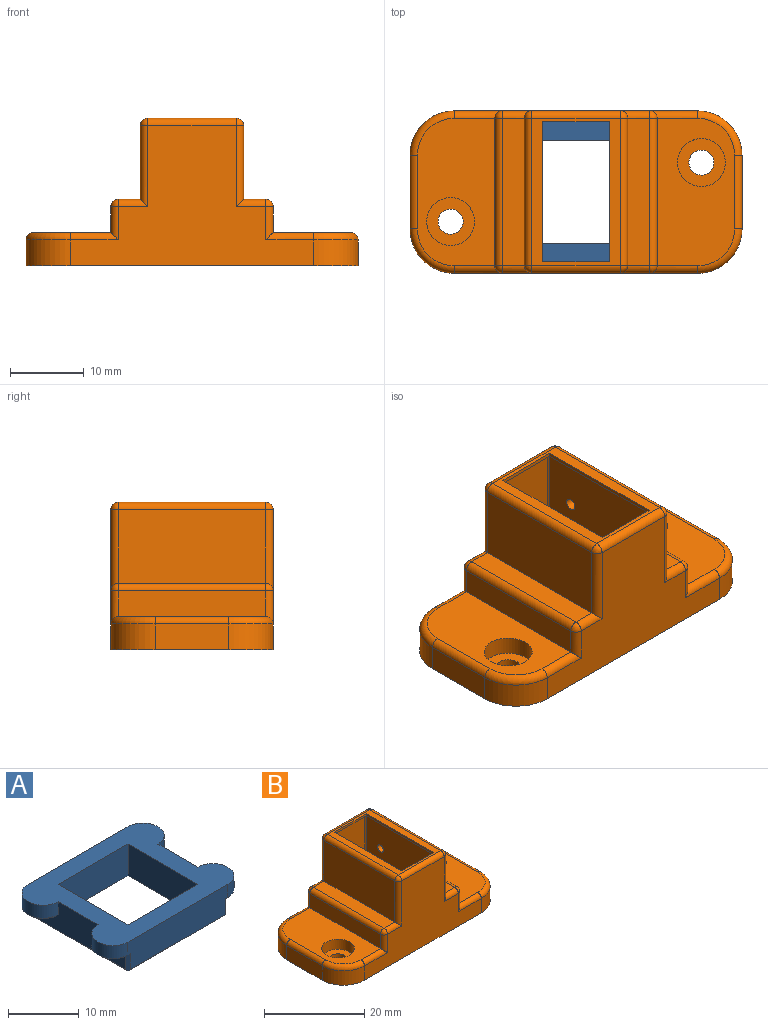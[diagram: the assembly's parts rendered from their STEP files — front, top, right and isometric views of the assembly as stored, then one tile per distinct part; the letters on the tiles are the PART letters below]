
ASSEMBLY  parts=2 mates=1
PART A: 42 faces, bbox 26x20x5.5 mm
  f0: plane 26x20mm, normal (0,0,1), area 260.5mm2, adj f5,f6,f7,f8,f9,f10,f11,f12
  f1: plane 19x19mm, normal (0,0,-1), area 165mm2, adj f22,f23,f24,f25,f26,f27,f28,f29
  f2: plane 5.5x3mm, normal (0,0,-1), area 8.1mm2, adj f12,f17,f31,f34,f35
  f3: plane 5.5x3mm, normal (0,0,-1), area 8.1mm2, adj f8,f15,f30,f38,f39
  f4: plane 5.5x3mm, normal (0,0,-1), area 8.1mm2, adj f8,f21,f32,f40,f41
  f5: cylinder r=3mm len=6mm, axis (0,0,-1), area 21.2mm2, adj f0,f6,f12,f36
  f6: plane 20x5mm, normal (0,1,0), area 97.2mm2, adj f0,f5,f7,f28,f32,f33,f37,f41
  f7: cylinder r=3mm len=6mm, axis (0,0,-1), area 21.2mm2, adj f0,f6,f8,f40
  f8: plane 19x5mm, normal (-1,0,0), area 67.6mm2, adj f0,f3,f4,f7,f9,f29,f30,f32
  f9: cylinder r=3mm len=6mm, axis (0,0,-1), area 21.2mm2, adj f0,f8,f10,f38
  f10: plane 20x5mm, normal (0,-1,0), area 97.2mm2, adj f0,f9,f11,f27,f30,f31,f35,f39
  f11: cylinder r=3mm len=6mm, axis (0,0,-1), area 21.2mm2, adj f0,f10,f12,f34
  f12: plane 19x5mm, normal (1,0,0), area 67.6mm2, adj f0,f2,f5,f11,f13,f26,f31,f33
  f13: plane 5.5x3mm, normal (0,0,-1), area 8.1mm2, adj f12,f19,f33,f36,f37
  f14: cone r=0mm half-angle=59deg, axis (0,0,-1), area 4.4mm2, adj f15
  f15: cylinder r=1.1mm len=2.2mm, axis (0,0,-1), area 3.5mm2, adj f3,f14
  f16: cone r=0mm half-angle=59deg, axis (0,0,-1), area 4.4mm2, adj f17
  f17: cylinder r=1.1mm len=2.2mm, axis (0,0,-1), area 3.5mm2, adj f2,f16
  f18: cone r=0mm half-angle=59deg, axis (0,0,-1), area 4.4mm2, adj f19
  f19: cylinder r=1.1mm len=2.2mm, axis (0,0,-1), area 3.5mm2, adj f13,f18
  f20: cone r=0mm half-angle=59deg, axis (0,0,-1), area 4.4mm2, adj f21
  f21: cylinder r=1.1mm len=2.2mm, axis (0,0,-1), area 3.5mm2, adj f4,f20
  f22: plane 14x5.5mm, normal (0,1,0), area 77mm2, adj f0,f1,f23,f25
  f23: plane 14x5.5mm, normal (-1,0,0), area 77mm2, adj f0,f1,f22,f24
  f24: plane 14x5.5mm, normal (0,-1,0), area 77mm2, adj f0,f1,f23,f25
  f25: plane 14x5.5mm, normal (1,0,0), area 77mm2, adj f0,f1,f22,f24
  f26: plane 19.5x0.5mm, normal (0.71,0,-0.71), area 13.6mm2, adj f1,f12,f27,f28,f31,f33
  f27: plane 19.5x0.5mm, normal (0,-0.71,-0.71), area 13.6mm2, adj f1,f10,f26,f29,f30,f31
  f28: plane 19.5x0.5mm, normal (0,0.71,-0.71), area 13.6mm2, adj f1,f6,f26,f29,f32,f33
  f29: plane 19.5x0.5mm, normal (-0.71,0,-0.71), area 13.6mm2, adj f1,f8,f27,f28,f30,f32
  f30: plane 3x0.5mm, normal (-0.71,-0.71,0), area 1.9mm2, adj f3,f8,f10,f27,f29,f39
  f31: plane 3x0.5mm, normal (0.71,-0.71,0), area 1.9mm2, adj f2,f10,f12,f26,f27,f35
  f32: plane 3x0.5mm, normal (-0.71,0.71,0), area 1.9mm2, adj f4,f6,f8,f28,f29,f41
  f33: plane 3x0.5mm, normal (0.71,0.71,0), area 1.9mm2, adj f6,f12,f13,f26,f28,f37
  f34: cone r=2.75mm half-angle=45deg, axis (0,0,1), area 3.2mm2, adj f2,f11,f12,f35
  f35: plane 0.5x0.25mm, normal (0,-0.71,-0.71), area 0.1mm2, adj f2,f10,f31,f34
  f36: cone r=3mm half-angle=45deg, axis (0,0,1), area 3.2mm2, adj f5,f12,f13,f37
  f37: plane 0.5x0.25mm, normal (0,0.71,-0.71), area 0.1mm2, adj f6,f13,f33,f36
  f38: cone r=3mm half-angle=45deg, axis (0,0,1), area 3.2mm2, adj f3,f8,f9,f39
  f39: plane 0.5x0.25mm, normal (0,-0.71,-0.71), area 0.1mm2, adj f3,f10,f30,f38
  f40: cone r=2.75mm half-angle=45deg, axis (0,0,1), area 3.2mm2, adj f4,f7,f8,f41
  f41: plane 0.5x0.25mm, normal (0,0.71,-0.71), area 0.1mm2, adj f4,f6,f32,f40
PART B: 111 faces, bbox 46x23x20 mm
  f0: plane 20x10.5mm, normal (0,0,1), area 166.1mm2, adj f33,f37,f69,f70,f72,f104,f106
  f1: plane 20x10.5mm, normal (0,0,1), area 166.1mm2, adj f36,f38,f85,f90,f94,f102,f108
  f2: plane 20x7.5mm, normal (1,0,0), area 112.1mm2, adj f3,f4,f5,f48,f57,f58,f59,f60
  f3: plane 45x22mm, normal (0,0,-1), area 453.5mm2, adj f2,f4,f5,f6,f7,f8,f9,f10
  f4: cylinder r=0.25mm len=7.5mm, axis (0,0,-1), area 7.9mm2, adj f2,f3,f12,f49,f59,f60
  f5: cylinder r=0.25mm len=7.5mm, axis (0,0,-1), area 7.9mm2, adj f2,f3,f11,f50,f57,f58
  f6: cylinder r=0.25mm len=7.5mm, axis (0,0,-1), area 7.9mm2, adj f3,f9,f10,f51,f55,f56
  f7: cylinder r=0.25mm len=7.5mm, axis (0,0,-1), area 7.9mm2, adj f3,f8,f9,f52,f53,f54
  f8: plane 7.5x4.75mm, normal (0,-1,0), area 35.6mm2, adj f3,f7,f15,f47
  f9: plane 20x7.5mm, normal (-1,0,0), area 112.1mm2, adj f3,f6,f7,f47,f53,f54,f55,f56
  f10: plane 7.5x4.75mm, normal (0,1,0), area 35.6mm2, adj f3,f6,f14,f47
  f11: plane 7.5x4.75mm, normal (0,-1,0), area 35.6mm2, adj f3,f5,f16,f48
  f12: plane 7.5x4.75mm, normal (0,1,0), area 35.6mm2, adj f3,f4,f13,f48
  f13: cylinder r=0.25mm len=19.5mm, axis (0,0,-1), area 20mm2, adj f3,f12,f19,f20,f43,f48
  f14: cylinder r=0.25mm len=19.5mm, axis (0,0,-1), area 20mm2, adj f3,f10,f18,f19,f44,f47
  f15: cylinder r=0.25mm len=19.5mm, axis (0,0,-1), area 20mm2, adj f3,f8,f17,f18,f45,f47
  f16: cylinder r=0.25mm len=19.5mm, axis (0,0,-1), area 20mm2, adj f3,f11,f17,f20,f46,f48
  f17: plane 19.5x9.5mm, normal (0,-1,0), area 185.2mm2, adj f3,f15,f16,f42
  f18: plane 20x12mm, normal (-1,0,0), area 236mm2, adj f14,f15,f42,f47,f109,f110
  f19: plane 19.5x9.5mm, normal (0,1,0), area 185.2mm2, adj f3,f13,f14,f42
  f20: plane 20x12mm, normal (1,0,0), area 240mm2, adj f13,f16,f42,f48
  f21: plane 9x0.5mm, normal (0,-1,0), area 4.5mm2, adj f22,f24,f25,f42
  f22: plane 19x0.5mm, normal (-1,0,0), area 9.5mm2, adj f21,f23,f25,f42
  f23: plane 9x0.5mm, normal (0,1,0), area 4.5mm2, adj f22,f24,f25,f42
  f24: plane 19x0.5mm, normal (1,0,0), area 9.5mm2, adj f21,f23,f25,f42
  f25: plane 20x12mm, normal (0,0,1), area 69mm2, adj f21,f22,f23,f24,f82,f83,f91,f92
  f26: plane 20x3mm, normal (0,0,1), area 60mm2, adj f41,f88,f96,f100
  f27: plane 33x19mm, normal (0,-1,0), area 337.5mm2, adj f3,f69,f71,f76,f78,f83,f84,f85
  f28: plane 10x3.5mm, normal (1,0,0), area 35mm2, adj f3,f70,f103,f105
  f29: plane 33x19mm, normal (0,1,0), area 337.5mm2, adj f3,f72,f74,f79,f81,f91,f94,f97
  f30: plane 10x3.5mm, normal (-1,0,0), area 35mm2, adj f3,f90,f101,f107
  f31: cylinder r=1.7mm len=3.4mm, axis (0,0,1), area 21.4mm2, adj f3,f32
  f32: plane 6.5x6.5mm, normal (0,0,1), area 24.1mm2, adj f31,f33
  f33: cylinder r=3.25mm len=6.5mm, axis (0,0,1), area 51.1mm2, adj f0,f32
  f34: cylinder r=1.7mm len=3.4mm, axis (0,0,1), area 21.4mm2, adj f3,f35
  f35: plane 6.5x6.5mm, normal (0,0,1), area 24.1mm2, adj f34,f36
  f36: cylinder r=3.25mm len=6.5mm, axis (0,0,1), area 51.1mm2, adj f1,f35
  f37: plane 20x3.5mm, normal (1,0,0), area 70mm2, adj f0,f71,f74,f75
  f38: plane 20x3.5mm, normal (-1,0,0), area 70mm2, adj f1,f89,f96,f97
  f39: plane 20x3mm, normal (0,0,1), area 60mm2, adj f40,f75,f76,f79
  f40: plane 20x10mm, normal (1,0,0), area 196mm2, adj f39,f78,f81,f82,f109,f110
  f41: plane 20x10mm, normal (-1,0,0), area 200mm2, adj f26,f84,f92,f98
  f42: plane 20.5x10mm, normal (0,0,-1), area 33.8mm2, adj f17,f18,f19,f20,f21,f22,f23,f24
  f43: cone r=0mm half-angle=59deg, axis (0,0,-1), area 0.2mm2, adj f13,f42
  f44: cone r=0mm half-angle=59deg, axis (0,0,-1), area 0.2mm2, adj f14,f42
  f45: cone r=0mm half-angle=59deg, axis (0,0,-1), area 0.2mm2, adj f15,f42
  f46: cone r=0mm half-angle=59deg, axis (0,0,-1), area 0.2mm2, adj f16,f42
  f47: plane 20.5x5.25mm, normal (0,0,-1), area 107.4mm2, adj f8,f9,f10,f14,f15,f18,f51,f52
  f48: plane 20.5x5.25mm, normal (0,0,-1), area 107.4mm2, adj f2,f11,f12,f13,f16,f20,f49,f50
  f49: cone r=0mm half-angle=59deg, axis (0,0,-1), area 0.2mm2, adj f4,f48
  f50: cone r=0mm half-angle=59deg, axis (0,0,-1), area 0.2mm2, adj f5,f48
  f51: cone r=0mm half-angle=59deg, axis (0,0,-1), area 0.2mm2, adj f6,f47
  f52: cone r=0mm half-angle=59deg, axis (0,0,-1), area 0.2mm2, adj f7,f47
  f53: cylinder r=3.25mm len=6.49mm, axis (0,0,-1), area 29.9mm2, adj f3,f7,f9,f54
  f54: plane 6.49x3.25mm, normal (0,0,-1), area 12.8mm2, adj f7,f9,f53,f68
  f55: cylinder r=3.25mm len=6.49mm, axis (0,0,-1), area 29.9mm2, adj f3,f6,f9,f56
  f56: plane 6.49x3.25mm, normal (0,0,-1), area 12.8mm2, adj f6,f9,f55,f66
  f57: cylinder r=3.25mm len=6.49mm, axis (0,0,-1), area 29.9mm2, adj f2,f3,f5,f58
  f58: plane 6.49x3.25mm, normal (0,0,-1), area 12.8mm2, adj f2,f5,f57,f64
  f59: cylinder r=3.25mm len=6.49mm, axis (0,0,-1), area 29.9mm2, adj f2,f3,f4,f60
  f60: plane 6.49x3.25mm, normal (0,0,-1), area 12.8mm2, adj f2,f4,f59,f62
  f61: cone r=0mm half-angle=59deg, axis (0,0,-1), area 4.4mm2, adj f62
  f62: cylinder r=1.1mm len=2.2mm, axis (0,0,-1), area 3.5mm2, adj f60,f61
  f63: cone r=0mm half-angle=59deg, axis (0,0,-1), area 4.4mm2, adj f64
  f64: cylinder r=1.1mm len=2.2mm, axis (0,0,-1), area 3.5mm2, adj f58,f63
  f65: cone r=0mm half-angle=59deg, axis (0,0,-1), area 4.4mm2, adj f66
  f66: cylinder r=1.1mm len=2.2mm, axis (0,0,-1), area 3.5mm2, adj f56,f65
  f67: cone r=0mm half-angle=59deg, axis (0,0,-1), area 4.4mm2, adj f68
  f68: cylinder r=1.1mm len=2.2mm, axis (0,0,-1), area 3.5mm2, adj f54,f67
  f69: cylinder r=1mm len=6.5mm, axis (-1,0,0), area 9.2mm2, adj f0,f27,f71,f106
  f70: cylinder r=1mm len=10mm, axis (0,-1,0), area 15.7mm2, adj f0,f28,f104,f106
  f71: cylinder r=1mm len=4.5mm, axis (0,0,1), area 6.1mm2, adj f27,f37,f69,f73
  f72: cylinder r=1mm len=6.5mm, axis (1,0,0), area 9.2mm2, adj f0,f29,f74,f104
  f73: sphere r=1mm, area 1.6mm2, adj f71,f75,f76
  f74: cylinder r=1mm len=4.5mm, axis (0,0,-1), area 6.1mm2, adj f29,f37,f72,f77
  f75: cylinder r=1mm len=20mm, axis (0,-1,0), area 31.4mm2, adj f37,f39,f73,f77
  f76: cylinder r=1mm len=4mm, axis (-1,0,0), area 5.3mm2, adj f27,f39,f73,f78
  f77: sphere r=1mm, area 1.6mm2, adj f74,f75,f79
  f78: cylinder r=1mm len=11mm, axis (0,0,1), area 16.3mm2, adj f27,f40,f76,f80
  f79: cylinder r=1mm len=4mm, axis (1,0,0), area 5.3mm2, adj f29,f39,f77,f81
  f80: sphere r=1mm, area 1.6mm2, adj f78,f82,f83
  f81: cylinder r=1mm len=11mm, axis (0,0,-1), area 16.3mm2, adj f29,f40,f79,f86
  f82: cylinder r=1mm len=20mm, axis (0,-1,0), area 31.4mm2, adj f25,f40,f80,f86
  f83: cylinder r=1mm len=12mm, axis (-1,0,0), area 18.8mm2, adj f25,f27,f80,f87
  f84: cylinder r=1mm len=11mm, axis (0,0,-1), area 16.3mm2, adj f27,f41,f87,f88
  f85: cylinder r=1mm len=6.5mm, axis (-1,0,0), area 9.2mm2, adj f1,f27,f89,f108
  f86: sphere r=1mm, area 1.6mm2, adj f81,f82,f91
  f87: sphere r=1mm, area 1.6mm2, adj f83,f84,f92
  f88: cylinder r=1mm len=4mm, axis (-1,0,0), area 5.3mm2, adj f26,f27,f84,f93
  f89: cylinder r=1mm len=4.5mm, axis (0,0,-1), area 6.1mm2, adj f27,f38,f85,f93
  f90: cylinder r=1mm len=10mm, axis (0,1,0), area 15.7mm2, adj f1,f30,f102,f108
  f91: cylinder r=1mm len=12mm, axis (1,0,0), area 18.8mm2, adj f25,f29,f86,f95
  f92: cylinder r=1mm len=20mm, axis (0,1,0), area 31.4mm2, adj f25,f41,f87,f95
  f93: sphere r=1mm, area 1.6mm2, adj f88,f89,f96
  f94: cylinder r=1mm len=6.5mm, axis (1,0,0), area 9.2mm2, adj f1,f29,f97,f102
  f95: sphere r=1mm, area 1.6mm2, adj f91,f92,f98
  f96: cylinder r=1mm len=20mm, axis (0,1,0), area 31.4mm2, adj f26,f38,f93,f99
  f97: cylinder r=1mm len=4.5mm, axis (0,0,1), area 6.1mm2, adj f29,f38,f94,f99
  f98: cylinder r=1mm len=11mm, axis (0,0,1), area 16.3mm2, adj f29,f41,f95,f100
  f99: sphere r=1mm, area 1.6mm2, adj f96,f97,f100
  f100: cylinder r=1mm len=4mm, axis (1,0,0), area 5.3mm2, adj f26,f29,f98,f99
  f101: cylinder r=6mm len=6mm, axis (0,0,1), area 33mm2, adj f3,f29,f30,f102
  f102: torus R=5mm, axis (0,0,1), area 13.9mm2, adj f1,f90,f94,f101
  f103: cylinder r=6mm len=6mm, axis (0,0,-1), area 33mm2, adj f3,f28,f29,f104
  f104: torus R=5mm, axis (0,0,1), area 13.9mm2, adj f0,f70,f72,f103
  f105: cylinder r=6mm len=6mm, axis (0,0,1), area 33mm2, adj f3,f27,f28,f106
  f106: torus R=5mm, axis (0,0,1), area 13.9mm2, adj f0,f69,f70,f105
  f107: cylinder r=6mm len=6mm, axis (0,0,-1), area 33mm2, adj f3,f27,f30,f108
  f108: torus R=5mm, axis (0,0,1), area 13.9mm2, adj f1,f85,f90,f107
  f109: cylinder r=0.8mm len=2mm, axis (1,0,0), area 10.1mm2, adj f18,f40
  f110: cylinder r=0.8mm len=2mm, axis (1,0,0), area 10.1mm2, adj f18,f40
PLACE A rot(axis=(0,1,0),180deg) t=(0.76,0,-15.63)mm
PLACE B t=(0.76,0,-19.13)mm
MATE slider B.f63 <-> A.f18  axis (0,0,-1) through (-10.74,7,-15.63)mm
